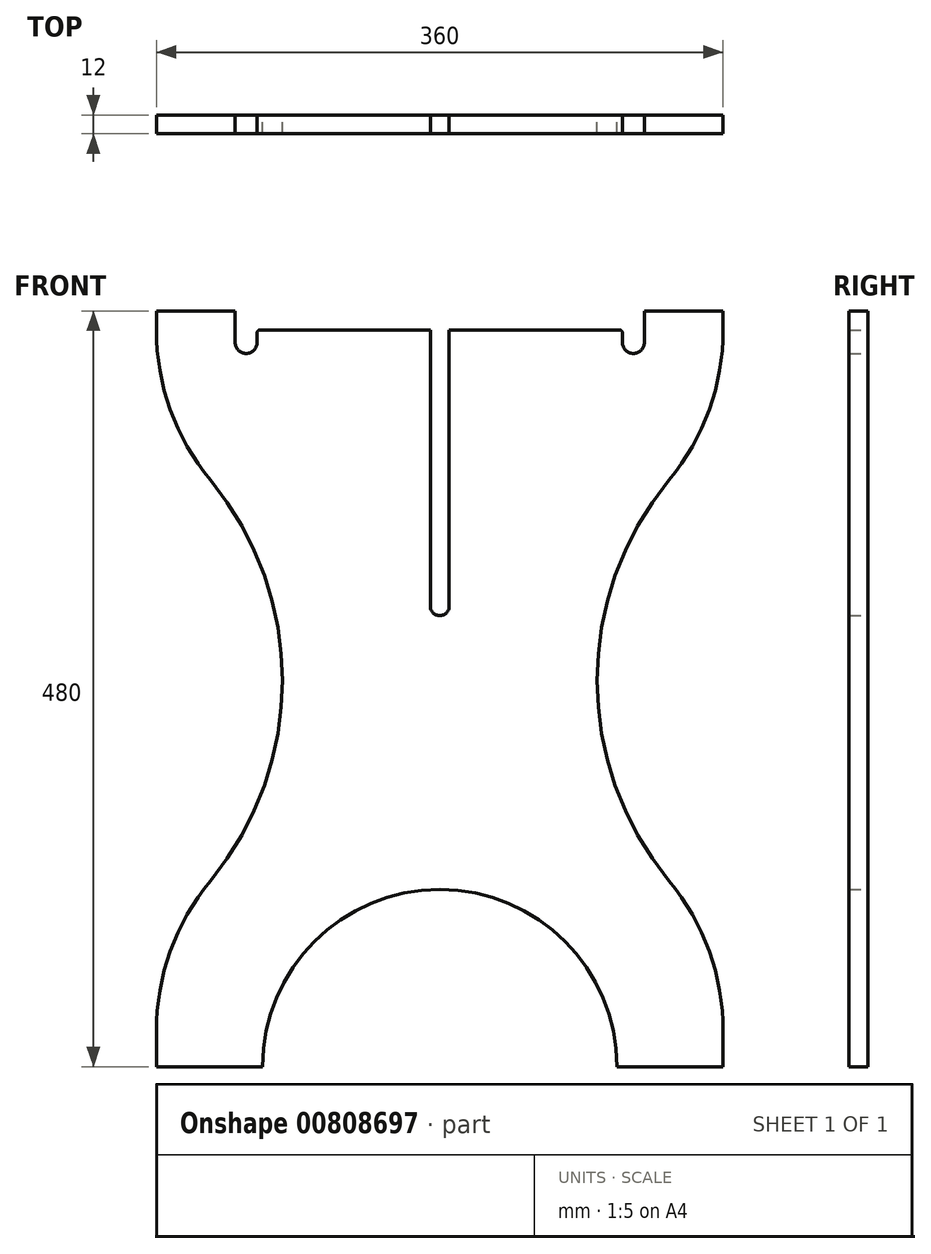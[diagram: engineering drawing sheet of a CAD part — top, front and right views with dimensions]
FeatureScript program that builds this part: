
annotation { "Feature Type Name" : "Feature", "Feature Type Description" : "" }
export const myFeature = defineFeature(function(context is Context, id is Id, definition is map)
    precondition{}
    {
        {
            var Q0;
            Q0=qCreatedBy(makeId("Front.planeOp"),FACE);
            var sketch = newSketch(context, id + "F0", { "sketchPlane" : qUnion([Q0])});
            skLineSegment(sketch, "E0.bottom", {"start": v(-180, -240) * mm, "end": v(-112.5, -240) * mm});
            skLineSegment(sketch, "E0.top", {"start": v(-180, 240) * mm, "end": v(-130, 240) * mm});
            skLineSegment(sketch, "E0.left", {"start": v(-180, -240) * mm, "end": v(-180, -217.42) * mm});
            skLineSegment(sketch, "E0.right", {"start": v(180, -240) * mm, "end": v(180, -217.42) * mm});
            skPoint(sketch, "E0.middle", {"position": v(0, 0) * mm});
            skLineSegment(sketch, "E1.0", {"start": v(-130, 228) * mm, "end": v(-130, 240) * mm});
            skLineSegment(sketch, "E2.0", {"start": v(130, 228) * mm, "end": v(130, 240) * mm});
            skLineSegment(sketch, "E3.trimOffspring", {"start": v(130, 240) * mm, "end": v(180, 240) * mm});
            skLineSegment(sketch, "E4.trimOffspring", {"start": v(112.5, -240) * mm, "end": v(180, -240) * mm});
            skArc(sketch, "E5", {"start": v(145.71, 132.55) * mm, "mid": v(100, 5.29) * mm, "end": v(145.71, -121.97) * mm});
            skArc(sketch, "E6", {"start": v(-145.71, -121.97) * mm, "mid": v(-100, 5.29) * mm, "end": v(-145.71, 132.55) * mm});
            skLineSegment(sketch, "E7.trimOffspring", {"start": v(-180, 228) * mm, "end": v(-180, 240) * mm});
            skLineSegment(sketch, "E8.trimOffspring", {"start": v(180, 228) * mm, "end": v(180, 240) * mm});
            skPoint(sketch, "E9.visualSharp", {"position": v(-180, 165.29) * mm});
            skArc(sketch, "E9.filletArc", {"start": v(-180, 228) * mm, "mid": v(-171.17, 177.3) * mm, "end": v(-145.71, 132.55) * mm});
            skPoint(sketch, "E10.visualSharp", {"position": v(-180, -154.71) * mm});
            skArc(sketch, "E10.filletArc", {"start": v(-145.71, -121.97) * mm, "mid": v(-171.17, -166.71) * mm, "end": v(-180, -217.42) * mm});
            skPoint(sketch, "E11.visualSharp", {"position": v(180, 165.29) * mm});
            skArc(sketch, "E11.filletArc", {"start": v(145.71, 132.55) * mm, "mid": v(171.17, 177.3) * mm, "end": v(180, 228) * mm});
            skPoint(sketch, "E12.visualSharp", {"position": v(180, -154.71) * mm});
            skArc(sketch, "E12.filletArc", {"start": v(180, -217.42) * mm, "mid": v(171.17, -166.71) * mm, "end": v(145.71, -121.97) * mm});
            skArc(sketch, "E13", {"start": v(116, 220) * mm, "mid": v(123, 213) * mm, "end": v(130, 220) * mm});
            skArc(sketch, "E14", {"start": v(-130, 220) * mm, "mid": v(-123, 213) * mm, "end": v(-116, 220) * mm});
            skLineSegment(sketch, "E15", {"start": v(-130, 228) * mm, "end": v(-130, 220) * mm});
            skLineSegment(sketch, "E16", {"start": v(-116, 220) * mm, "end": v(-116, 226) * mm});
            skLineSegment(sketch, "E17.trimOffspring", {"start": v(-114, 228) * mm, "end": v(-6, 228) * mm});
            skLineSegment(sketch, "E18", {"start": v(130, 228) * mm, "end": v(130, 220) * mm});
            skLineSegment(sketch, "E19", {"start": v(116, 220) * mm, "end": v(116, 226) * mm});
            skPoint(sketch, "E20.visualSharp", {"position": v(-115.99, 228) * mm});
            skArc(sketch, "E20.filletArc", {"start": v(-114, 228) * mm, "mid": v(-115.4, 227.42) * mm, "end": v(-116, 226) * mm});
            skPoint(sketch, "E21.visualSharp", {"position": v(116, 228) * mm});
            skArc(sketch, "E21.filletArc", {"start": v(116, 226) * mm, "mid": v(115.41, 227.41) * mm, "end": v(114, 228) * mm});
            skArc(sketch, "E22.MirrorCS", {"start": v(6, 52.5) * mm, "mid": v(0, 46.5) * mm, "end": v(-6, 52.5) * mm});
            skLineSegment(sketch, "E23.MirrorCS", {"start": v(-6, 228) * mm, "end": v(-6, 52.5) * mm});
            skLineSegment(sketch, "E24.MirrorCS", {"start": v(6, 228) * mm, "end": v(6, 52.5) * mm});
            skArc(sketch, "E25", {"start": v(112.5, -240) * mm, "mid": v(0, -127.5) * mm, "end": v(-112.5, -240) * mm});
            skLineSegment(sketch, "E26.trimOffspring", {"start": v(6, 228) * mm, "end": v(114, 228) * mm});
            skPoint(sketch, "E27.MirrorCS.end.orphan", {"position": v(6, 52.5) * mm});
            skSolve(sketch);
        }
        {
            var Q0;
            Q0=makeQuery(id+"F0.imprint","IMPRINT",FACE,{"disambiguationData":[TD([[makeQuery(id+"F0.imprint","IMPRINT",EDGE,{"derivedFrom":sQuery(id+"F0.wireOp",EDGE,"E0.bottom")}),1.0]])]});
            extrude(context, id + "F1", {"entities" : qUnion([Q0]), "depth" : 12 * mm, "offsetDistance" : 25 * mm});
        }
    });
